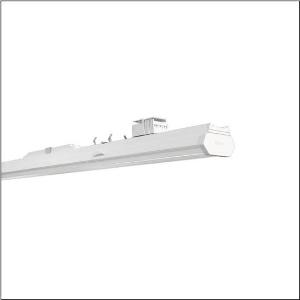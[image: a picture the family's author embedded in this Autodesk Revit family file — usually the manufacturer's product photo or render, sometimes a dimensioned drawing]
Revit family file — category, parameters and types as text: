
# Revit family: licross_r__11_protected_ho_51td12dn4fxm3s4_da94
name_source: partatom
category: Lighting Fixtures
units: mm (PartAtom-declared; Revit-internal decimal feet)

## family parameters
Cut with Voids When Loaded = No
Host = Face
Light Source = No
Part Type = Normal
Room Calculation Point = No
Round Connector Dimension = Use Diameter
Shared = No

## types (1)
- --- (1 x LED, 970 lm, 7.4 W, 4000K)
    Apparent Load = 7 VA
    CIE Flux Codes = 70 91 97 98 100
    Color Rendering = 80
    Color Temperature = 4000K
    Default Elevation = 1800 mm
    Description = Licross® 11 Protected HO, luminaire insert, of sheet steel, galvanised, coil coated, white, length: 1.500mm, width: 90mm, height: 101mm, LED rated luminous flux: 15.270lm, light colour: 840, control gear: DALI 2, with plug, 6-pole, with phase selection, for trunking rail, 9 or 11-core, mains connection: 220..240V, AC, 50/60Hz, rated input power: 91W, for trunking rail, 9-/11-core, halogen-free wiring, for emergency light function, converter,control gear: single battery element, battery: LiFeP04, 9Ah, primary light control with lens, of plastic, primary optical cover: cover, of PMMA, light emission: direct distribution, primary light characteristic: symmetric, protection rating (complete): IP54, insulation class (complete): insulation class I (protective earthing), certification: CE, UKCA, protection symbol: D if used in an environment with non-conductive dust loads with corresponding accessories, impact resistance: IK06, permissible ambient temperature for indoor applications: +5..+30°C, standard: EN 60598-2-22, LABS conformity tested according to VDMA 24364:2018-05, reducing of maximum allowable ambient temperature of 5°C with ceiling mounting, corresponds to IFS (International Featured Standards) requirements for safety and quality in the food industry, packaging unit: 1 piece
    Height = 92 mm
    Lamp = 1 x LED
    Lamp Light Flux = 970 lm
    Lamp Power = 7.4 W
    Lamp count = 1
    Length = 1500 mm
    Luminous efficacy = 131 lm/W
    Manufacturer = Siteco
    ModVariant = No
    Model = 51TD12DN4FXM3S4
    Mounting Place = Ceiling
    Mounting Type = Pendant
    Number of Poles = 1
    OnlyDefault = Yes
    Power Factor = 1
    Product Name = Licross® 11 Protected HO
    Product group = luminaire insert
    ProductGroupID = 901
    Protection Class = Protection class I
    Protection Degree = IP 54
    RLX_Detail_Level = 1
    RLX_Emergency_Light_Flux = 0 lm
    RLX_Emergency_Type = 0
    RLX_Emergency_Type_DB = No
    RlxData = <blob elided: 24917 chars, md5=b2197794>
    Socket = socket
    Standby Power = 0 W
    System Light Flux = 970 lm
    System Power = 7 W
    Type Comments = : emergency light operation: 3 h
    Type Image = l_1256145.jpg
    URL = http://relux.com
    VarID = @adj_041393
    Voltage = 0 V
    Weight = 0.00 kg
    Width = 88 mm

## geometry (parser evidence)
native form markers: Blend x4, Sweep x11
no freeform markers — native parametric forms only
